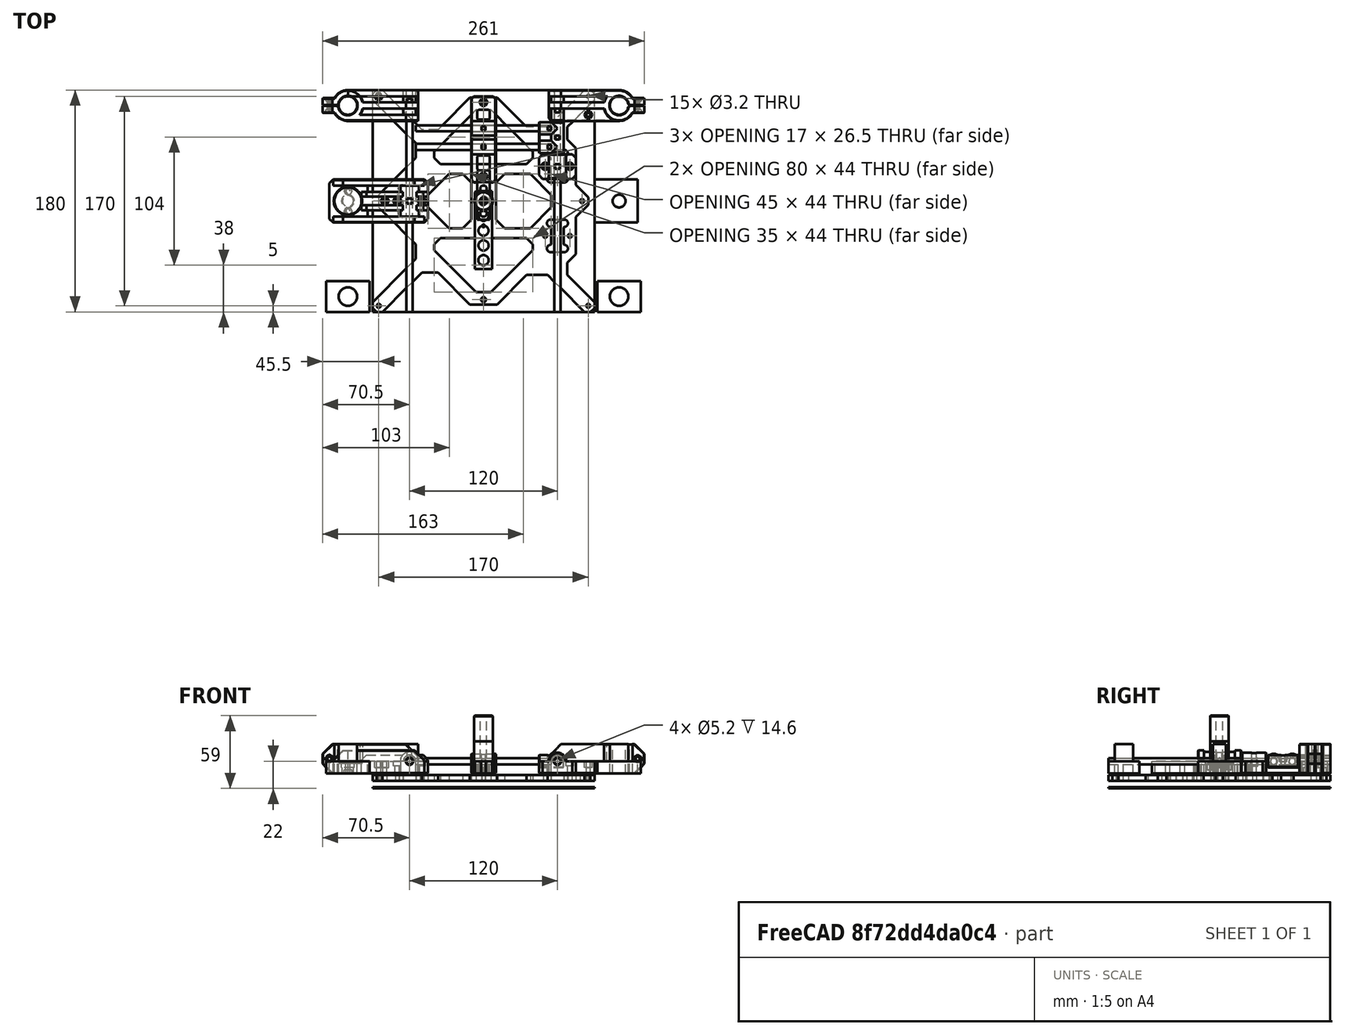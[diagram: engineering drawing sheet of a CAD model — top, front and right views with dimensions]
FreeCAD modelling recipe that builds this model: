
FCSTD DOCUMENT  (FreeCAD 0.18R16146 (Git))
Label: mini-bed
License: All rights reserved
LicenseURL: http://en.wikipedia.org/wiki/All_rights_reserved
objects: Part::Cylinder×73, Part::Chamfer×40, Part::Box×32, Part::Cut×28, Part::MultiFuse×22, Part::Feature×9
note: 204 computed .brp shape members not serialized (recipe doc carries the construction recipe); baked Part::Feature solids carry a one-line shape summary decoded from their .brp

FEATURE [Part::Feature] Part__Feature  label="carrier"
  Placement = pos=(0,0,-1) rot=(0,1,0;3.14159rad)
  shape: bbox 180 x 180 x 5 mm, 131 faces (baked)
FEATURE [Part::Cylinder] Cylinder
  Angle = 360
  AttacherType = Attacher::AttachEngine3D
  Height = 24
  Placement = pos=(-110,0,0) rot=(0,0,1;0rad)
  Radius = 4.5
FEATURE [Part::Cylinder] Cylinder001
  Angle = 360
  AttacherType = Attacher::AttachEngine3D
  Height = 24
  Placement = pos=(110,0,0) rot=(0,0,1;0rad)
  Radius = 5.2
FEATURE [Part::Cylinder] Cylinder002
  Angle = 360
  AttacherType = Attacher::AttachEngine3D
  Height = 24
  Placement = pos=(-110,77.5,0) rot=(0,0,1;0rad)
  Radius = 7.5
FEATURE [Part::Cylinder] Cylinder003
  Angle = 360
  AttacherType = Attacher::AttachEngine3D
  Height = 24
  Placement = pos=(-110,-77.5,0) rot=(0,0,1;0rad)
  Radius = 7.5
FEATURE [Part::Cylinder] Cylinder005
  Angle = 360
  AttacherType = Attacher::AttachEngine3D
  Height = 24
  Placement = pos=(110,-77.5,0) rot=(0,0,1;0rad)
  Radius = 7.5
FEATURE [Part::Cylinder] Cylinder007
  Angle = 360
  AttacherType = Attacher::AttachEngine3D
  Height = 30
  Placement = pos=(0,80,0) rot=(0,0,1;0rad)
  Radius = 1.65
FEATURE [Part::Cylinder] Cylinder008
  Angle = 360
  AttacherType = Attacher::AttachEngine3D
  Height = 10
  Placement = pos=(0,-80,0) rot=(0,0,1;0rad)
  Radius = 2
FEATURE [Part::Box] Box  label="bed"
  AttacherType = Attacher::AttachEngine3D
  Height = 1
  Length = 180
  Placement = pos=(-90,-90,-12) rot=(0,0,1;0rad)
  Width = 180
FEATURE [Part::Box] Box001  label="Cube"
  AttacherType = Attacher::AttachEngine3D
  Height = 10
  Length = 57
  Placement = pos=(-110,65,0) rot=(0,0,1;0rad)
  Width = 25
FEATURE [Part::Box] Box002  label="Cube001"
  AttacherType = Attacher::AttachEngine3D
  Height = 10
  Length = 35
  Placement = pos=(-127.5,-90,0) rot=(0,0,1;0rad)
  Width = 25
FEATURE [Part::Box] Box003  label="Cube002"
  AttacherType = Attacher::AttachEngine3D
  Height = 10
  Length = 35
  Placement = pos=(92.5,-90,0) rot=(0,0,1;0rad)
  Width = 25
FEATURE [Part::Box] Box005  label="Cube004"
  AttacherType = Attacher::AttachEngine3D
  Height = 10
  Length = 80
  Placement = pos=(-125,-17.5,0) rot=(0,0,1;0rad)
  Width = 35
FEATURE [Part::Box] Box006  label="Cube005"
  AttacherType = Attacher::AttachEngine3D
  Height = 10
  Length = 35
  Placement = pos=(90,-17.5,0) rot=(0,0,1;0rad)
  Width = 35
FEATURE [Part::Cylinder] Cylinder011
  Angle = 360
  AttacherType = Attacher::AttachEngine3D
  Height = 180
  Placement = pos=(-60,-90,10) rot=(-1,0,0;1.5708rad)
  Radius = 2.5
FEATURE [Part::Cylinder] Cylinder012
  Angle = 360
  AttacherType = Attacher::AttachEngine3D
  Height = 180
  Placement = pos=(60,-90,10) rot=(-1,0,0;1.5708rad)
  Radius = 2.5
FEATURE [Part::Cylinder] Cylinder013
  Angle = 360
  AttacherType = Attacher::AttachEngine3D
  Height = 24
  Placement = pos=(-110,77.5,0) rot=(0,0,1;0rad)
  Radius = 12.5
FEATURE [Part::Box] Box007  label="Cube006"
  AttacherType = Attacher::AttachEngine3D
  Height = 24
  Length = 57
  Placement = pos=(-110,65,0) rot=(0,0,1;0rad)
  Width = 5
FEATURE [Part::Box] Box008  label="Cube007"
  AttacherType = Attacher::AttachEngine3D
  Height = 24
  Length = 57
  Placement = pos=(-110,85,0) rot=(0,0,1;0rad)
  Width = 5
FEATURE [Part::Box] Box009  label="Cube008"
  AttacherType = Attacher::AttachEngine3D
  Height = 24
  Length = 49
  Placement = pos=(-102,75,0) rot=(0,0,1;0rad)
  Width = 5
FEATURE [Part::Cylinder] Cylinder014
  Angle = 360
  AttacherType = Attacher::AttachEngine3D
  Height = 25
  Placement = pos=(-60,65,10) rot=(-1,0,0;1.5708rad)
  Radius = 5
FEATURE [Part::Cylinder] Cylinder015
  Angle = 360
  AttacherType = Attacher::AttachEngine3D
  Height = 70
  Placement = pos=(-85,85,0) rot=(0,0,1;0rad)
  Radius = 1.65
FEATURE [Part::Box] Box010  label="Cube009"
  AttacherType = Attacher::AttachEngine3D
  Height = 24
  Length = 12
  Placement = pos=(-130.5,71.5,0) rot=(0,0,1;0rad)
  Width = 12
FEATURE [Part::Chamfer] Chamfer
  Base = -> Box007
  Edges = 1 edges r=10: [Edge6]
FEATURE [Part::Chamfer] Chamfer001
  Base = -> Box009
  Edges = 1 edges r=10: [Edge6]
FEATURE [Part::Chamfer] Chamfer002
  Base = -> Box010
  Edges = 2 edges r=8: [Edge2,Edge4]
FEATURE [Part::Chamfer] Chamfer003
  Base = -> Chamfer002
  Edges = 10 edges r=0.4: [Edge1,Edge4,Edge5,Edge6,Edge8,Edge9,Edge11,Edge13,Edge14,Edge16]
FEATURE [Part::Cylinder] Cylinder016
  Angle = 360
  AttacherType = Attacher::AttachEngine3D
  Height = 24
  Placement = pos=(-110,77.5,0) rot=(0,0,1;0rad)
  Radius = 7.5
FEATURE [Part::Feature] Body001  label="hex-nut"
  shape: bbox 5.543 x 6.4 x 5 mm, 8 faces (baked)
FEATURE [Part::Feature] Body002  label="hex-nut001"
  Placement = pos=(-85,85,5) rot=(0,0,-1;1.5708rad)
  shape: bbox 6.4 x 5.543 x 5 mm, 8 faces (baked)
FEATURE [Part::Feature] Body003  label="hex-nut002"
  Placement = pos=(-125,81,12) rot=(0,0.707107,0.707107;3.14159rad)
  shape: bbox 5.543 x 5 x 6.4 mm, 8 faces (baked)
FEATURE [Part::Cut] Cut
  Base = -> Chamfer003
  Tool = -> Body003
FEATURE [Part::Cut] Cut001
  Base = -> Box001
  Tool = -> Body002
FEATURE [Part::Cut] Cut002
  Base = -> Cut001
  Tool = -> Cylinder015
FEATURE [Part::Chamfer] Chamfer004
  Base = -> Cut002
  Edges = 1 edges r=2: [Edge17]
FEATURE [Part::Chamfer] Chamfer005
  Base = -> Cylinder013
  Edges = 2 edges r=0.4: [Edge1,Edge3]
FEATURE [Part::MultiFuse] Fusion001
  Shapes = -> [Chamfer004,Chamfer001,Chamfer]
FEATURE [Part::Chamfer] Chamfer006
  Base = -> Fusion001
  Edges = 11 edges r=0.4: [Edge16,Edge19,Edge31,Edge40,Edge59,Edge63,Edge64,Edge65,Edge67,Edge70,Edge76]
FEATURE [Part::Cylinder] Cylinder017
  Angle = 360
  AttacherType = Attacher::AttachEngine3D
  Height = 3
  Placement = pos=(-125,71,12) rot=(-1,0,0;1.5708rad)
  Radius = 3
FEATURE [Part::Cylinder] Cylinder018
  Angle = 360
  AttacherType = Attacher::AttachEngine3D
  Height = 21
  Placement = pos=(-125,68,12) rot=(-1,0,0;1.5708rad)
  Radius = 1.65
FEATURE [Part::Cylinder] Cylinder019
  Angle = 360
  AttacherType = Attacher::AttachEngine3D
  Height = 21
  Placement = pos=(-125,68,13.4) rot=(-1,0,0;1.5708rad)
  Radius = 0.5
FEATURE [Part::MultiFuse] Fusion002
  Shapes = -> [Cylinder019,Cylinder018]
FEATURE [Part::Cut] Cut003
  Base = -> Cut
  Tool = -> Fusion002
FEATURE [Part::Cylinder] Cylinder020
  Angle = 360
  AttacherType = Attacher::AttachEngine3D
  Height = 3
  Placement = pos=(-125,71,14.7) rot=(-1,0,0;1.5708rad)
  Radius = 0.5
FEATURE [Part::MultiFuse] Fusion003
  Shapes = -> [Cylinder020,Cylinder017]
FEATURE [Part::Cut] Cut004
  Base = -> Cut003
  Tool = -> Fusion003
FEATURE [Part::Box] Box012  label="Cube011"
  AttacherType = Attacher::AttachEngine3D
  Height = 36
  Length = 22
  Placement = pos=(-135,77.25,0) rot=(0,0,1;0rad)
  Width = 0.5
FEATURE [Part::Cylinder] Cylinder021  label="rod-slot-1"
  Angle = 360
  AttacherType = Attacher::AttachEngine3D
  Height = 25
  Placement = pos=(-60,65,10) rot=(-1,0,0;1.5708rad)
  Radius = 2.6
FEATURE [Part::Cylinder] Cylinder022
  Angle = 360
  AttacherType = Attacher::AttachEngine3D
  Height = 3
  Placement = pos=(-60,80,10) rot=(-1,0,0;1.5708rad)
  Radius = 3
FEATURE [Part::Box] Box013  label="Cube012"
  AttacherType = Attacher::AttachEngine3D
  Height = 10
  Length = 4
  Placement = pos=(-62,80,9) rot=(0,0,1;0rad)
  Width = 3
FEATURE [Part::Cylinder] Cylinder023
  Angle = 360
  AttacherType = Attacher::AttachEngine3D
  Height = 27
  Placement = pos=(-80,0,0) rot=(0,0,1;0rad)
  Radius = 1.65
FEATURE [Part::Cylinder] Cylinder024
  Angle = 360
  AttacherType = Attacher::AttachEngine3D
  Height = 27
  Placement = pos=(-70,0,0) rot=(0,0,1;0rad)
  Radius = 1.65
FEATURE [Part::Cylinder] Cylinder025
  Angle = 360
  AttacherType = Attacher::AttachEngine3D
  Height = 27
  Placement = pos=(-50,0,0) rot=(0,0,1;0rad)
  Radius = 1.65
FEATURE [Part::Cylinder] Cylinder026
  Angle = 360
  AttacherType = Attacher::AttachEngine3D
  Height = 2
  Placement = pos=(-110,0,8) rot=(0,0,1;0rad)
  Radius = 11.5
FEATURE [Part::Cylinder] Cylinder027
  Angle = 360
  AttacherType = Attacher::AttachEngine3D
  Height = 10
  Placement = pos=(-110,8,0) rot=(0,0,1;0rad)
  Radius = 1.65
FEATURE [Part::Cylinder] Cylinder028
  Angle = 360
  AttacherType = Attacher::AttachEngine3D
  Height = 10
  Placement = pos=(-110,-8,0) rot=(0,0,1;0rad)
  Radius = 1.65
FEATURE [Part::Feature] Body004  label="hex-nut003"
  Placement = pos=(-110,8,-2) rot=(0,0,-1;4.71239rad)
  shape: bbox 6.4 x 5.543 x 5 mm, 8 faces (baked)
FEATURE [Part::Feature] Body005  label="hex-nut004"
  Placement = pos=(-110,-8,-2) rot=(0,0,1;1.5708rad)
  shape: bbox 6.4 x 5.543 x 5 mm, 8 faces (baked)
FEATURE [Part::Cylinder] Cylinder029
  Angle = 360
  AttacherType = Attacher::AttachEngine3D
  Height = 24
  Placement = pos=(-110,0,5) rot=(0,0,1;0rad)
  Radius = 5.2
FEATURE [Part::Cut] Cut009
  Base = -> Box005
  Tool = -> Cylinder029
FEATURE [Part::Cylinder] Cylinder030
  Angle = 360
  AttacherType = Attacher::AttachEngine3D
  Height = 35
  Placement = pos=(-60,-17.5,10) rot=(-1,0,0;1.5708rad)
  Radius = 7.5
FEATURE [Part::Cylinder] Cylinder031  label="rod-slot-2"
  Angle = 360
  AttacherType = Attacher::AttachEngine3D
  Height = 35
  Placement = pos=(-60,-17.5,10) rot=(-1,0,0;1.5708rad)
  Radius = 2.6
FEATURE [Part::Box] Box014  label="Cube013"
  AttacherType = Attacher::AttachEngine3D
  Height = 5
  Length = 54
  Placement = pos=(-99,-7.5,10) rot=(0,0,1;0rad)
  Width = 4
FEATURE [Part::Box] Box015  label="Cube014"
  AttacherType = Attacher::AttachEngine3D
  Height = 9
  Length = 74
  Placement = pos=(-122,12.5,10) rot=(0,0,1;0rad)
  Width = 5
FEATURE [Part::Feature] Body006  label="hex-nut005"
  Placement = pos=(-80,0,5) rot=(0,0,-1;1.5708rad)
  shape: bbox 6.4 x 5.543 x 5 mm, 8 faces (baked)
FEATURE [Part::Box] Box016  label="Cube015"
  AttacherType = Attacher::AttachEngine3D
  Height = 9
  Length = 74
  Placement = pos=(-122,-17.5,10) rot=(0,0,1;0rad)
  Width = 5
FEATURE [Part::Box] Box017  label="Cube016"
  AttacherType = Attacher::AttachEngine3D
  Height = 5
  Length = 54
  Placement = pos=(-99,3.5,10) rot=(0,0,1;0rad)
  Width = 4
FEATURE [Part::Chamfer] Chamfer012
  Base = -> Box015
  Edges = 2 edges r=8: [Edge2,Edge6]
FEATURE [Part::Chamfer] Chamfer013
  Base = -> Box016
  Edges = 2 edges r=8: [Edge2,Edge6]
FEATURE [Part::Chamfer] Chamfer014
  Base = -> Box017
  Edges = 2 edges r=4: [Edge2,Edge6]
FEATURE [Part::Chamfer] Chamfer015
  Base = -> Box014
  Edges = 2 edges r=4: [Edge2,Edge6]
FEATURE [Part::Chamfer] Chamfer016
  Base = -> Chamfer013
  Edges = 5 edges r=0.4: [Edge1,Edge5,Edge6,Edge8,Edge9]
FEATURE [Part::Chamfer] Chamfer017
  Base = -> Chamfer012
  Edges = 5 edges r=0.4: [Edge4,Edge11,Edge14,Edge15,Edge16]
FEATURE [Part::Cylinder] Cylinder032
  Angle = 360
  AttacherType = Attacher::AttachEngine3D
  Height = 12
  Placement = pos=(-70,0,6) rot=(0,0,1;0rad)
  Radius = 3
FEATURE [Part::Cylinder] Cylinder033
  Angle = 360
  AttacherType = Attacher::AttachEngine3D
  Height = 12
  Placement = pos=(-50,0,6) rot=(0,0,1;0rad)
  Radius = 3
FEATURE [Part::Cylinder] Cylinder034
  Angle = 360
  AttacherType = Attacher::AttachEngine3D
  Height = 5
  Placement = pos=(-60,-2.5,10) rot=(-1,0,0;1.5708rad)
  Radius = 3
FEATURE [Part::MultiFuse] Fusion009
  Shapes = -> [Box013,Cylinder022]
FEATURE [Part::Box] Box018  label="Cube017"
  AttacherType = Attacher::AttachEngine3D
  Height = 10
  Length = 4
  Placement = pos=(-62,-2,11) rot=(0,0,1;0rad)
  Width = 4
FEATURE [Part::Cylinder] Cylinder035
  Angle = 360
  AttacherType = Attacher::AttachEngine3D
  Height = 4
  Placement = pos=(50,28.25,0) rot=(0,0,1;0rad)
  Radius = 3
FEATURE [Part::Cylinder] Cylinder036
  Angle = 360
  AttacherType = Attacher::AttachEngine3D
  Height = 4
  Placement = pos=(70,28.25,0) rot=(0,0,1;0rad)
  Radius = 3
FEATURE [Part::Box] Box019  label="Cube018"
  AttacherType = Attacher::AttachEngine3D
  Height = 10
  Length = 30
  Placement = pos=(45,18,0) rot=(0,0,1;0rad)
  Width = 20
FEATURE [Part::Cylinder] Cylinder037
  Angle = 360
  AttacherType = Attacher::AttachEngine3D
  Height = 20
  Placement = pos=(60,18,10) rot=(-1,0,0;1.5708rad)
  Radius = 7
FEATURE [Part::Cylinder] Cylinder038  label="rod-slot-3"
  Angle = 360
  AttacherType = Attacher::AttachEngine3D
  Height = 20
  Placement = pos=(60,18,10) rot=(-1,0,0;1.5708rad)
  Radius = 2.6
FEATURE [Part::Chamfer] Chamfer019
  Base = -> Box019
  Edges = 4 edges r=3: [Edge1,Edge3,Edge5,Edge7]
FEATURE [Part::Cylinder] Cylinder039
  Angle = 360
  AttacherType = Attacher::AttachEngine3D
  Height = 33
  Placement = pos=(50,28.25,0) rot=(0,0,1;0rad)
  Radius = 1.65
FEATURE [Part::Cylinder] Cylinder040
  Angle = 360
  AttacherType = Attacher::AttachEngine3D
  Height = 33
  Placement = pos=(70,28.25,0) rot=(0,0,1;0rad)
  Radius = 1.65
FEATURE [Part::MultiFuse] Fusion010
  Shapes = -> [Cylinder040,Cylinder039]
FEATURE [Part::Cut] Cut024
  Base = -> Chamfer019
  Tool = -> Fusion010
FEATURE [Part::MultiFuse] Fusion011
  Placement = pos=(0,0,6) rot=(0,0,1;0rad)
  Shapes = -> [Cylinder035,Cylinder036]
FEATURE [Part::Chamfer] Chamfer020
  Base = -> Cylinder037
  Edges = 2 edges r=0.4: [Edge1,Edge3]
FEATURE [Part::Chamfer] Chamfer021
  Base = -> Cut024
  Edges = 10 edges r=0.4: [Edge4,Edge14,Edge16,Edge18,Edge19,Edge20,Edge21,Edge22,Edge23,Edge24]
FEATURE [Part::Cut] Cut025
  Base = -> Chamfer021
  Tool = -> Fusion011
FEATURE [Part::MultiFuse] Fusion012
  Shapes = -> [Cut025,Chamfer020]
FEATURE [Part::Cylinder] Cylinder041  label="cut"
  Angle = 360
  AttacherType = Attacher::AttachEngine3D
  Height = 4
  Placement = pos=(60,26.25,10) rot=(-1,0,0;1.5708rad)
  Radius = 3
FEATURE [Part::Box] Box020  label="Cube019"
  AttacherType = Attacher::AttachEngine3D
  Height = 10
  Length = 4
  Placement = pos=(58,26,10) rot=(0,0,1;0rad)
  Width = 4
FEATURE [Part::Cut] Cut026
  Base = -> Fusion012
  Tool = -> Cylinder041
FEATURE [Part::Cut] Cut027
  Base = -> Cut026
  Tool = -> Box020
FEATURE [Part::Chamfer] Chamfer007
  Base = -> Cylinder014
  Edges = 1 edges r=0.4: [Edge1]
FEATURE [Part::MultiFuse] Fusion006
  Shapes = -> [Chamfer005,Chamfer006,Chamfer007,Cut004]
FEATURE [Part::Cut] Cut005
  Base = -> Fusion006
  Tool = -> Cylinder016
FEATURE [Part::Cut] Cut006
  Base = -> Cut005
  Tool = -> Box012
FEATURE [Part::Chamfer] Chamfer008
  Base = -> Cut006
  Edges = 2 edges r=1: [Edge33,Edge49]
FEATURE [Part::Chamfer] Chamfer009
  Base = -> Chamfer008
  Edges = 11 edges r=0.4: [Edge2,Edge4,Edge21,Edge23,Edge24,Edge26,Edge55,Edge59,Edge61,Edge62,Edge102]
FEATURE [Part::Cut] Cut021
  Base = -> Chamfer009
  Tool = -> Fusion009
FEATURE [Part::Cylinder] Cylinder042  label="Cylinder041"
  Angle = 360
  AttacherType = Attacher::AttachEngine3D
  Height = 26.5
  Radius = 7.5
FEATURE [Part::Cylinder] Cylinder043  label="Cylinder042"
  Angle = 360
  AttacherType = Attacher::AttachEngine3D
  Height = 26.5
  Radius = 2.65
FEATURE [Part::Cylinder] Cylinder044  label="Cylinder045"
  Angle = 360
  AttacherType = Attacher::AttachEngine3D
  Height = 47
  Radius = 2.65
FEATURE [Part::Cylinder] Cylinder045  label="Cylinder046"
  Angle = 360
  AttacherType = Attacher::AttachEngine3D
  Height = 47
  Radius = 7.5
FEATURE [Part::Cut] Cut031
  Base = -> Cylinder045
  Tool = -> Cylinder044
FEATURE [Part::Chamfer] Chamfer025  label="long-rod"
  Base = -> Cut031
  Edges = 4 edges r=0.4: [Edge1,Edge3,Edge4,Edge5]
FEATURE [Part::Cut] Cut032
  Base = -> Cylinder042
  Tool = -> Cylinder043
FEATURE [Part::Chamfer] Chamfer026  label="short-rod"
  Base = -> Cut032
  Edges = 4 edges r=0.4: [Edge1,Edge3,Edge4,Edge5]
FEATURE [Part::MultiFuse] Fusion013
  Shapes = -> [Cylinder034,Box018]
FEATURE [Part::MultiFuse] Fusion014
  Shapes = -> [Body004,Cylinder027,Cylinder,Body005,Cylinder028,Cylinder026]
FEATURE [Part::Chamfer] Chamfer027
  Base = -> Cut009
  Edges = 4 edges r=3: [Edge1,Edge3,Edge6,Edge12]
FEATURE [Part::Chamfer] Chamfer028
  Base = -> Chamfer027
  Edges = 8 edges r=0.4: [Edge4,Edge13,Edge15,Edge17,Edge18,Edge19,Edge20,Edge21]
FEATURE [Part::MultiFuse] Fusion016
  Shapes = -> [Chamfer028,Chamfer017,Chamfer014,Cylinder030,Chamfer015,Chamfer016]
FEATURE [Part::Cut] Cut033
  Base = -> Fusion016
  Tool = -> Fusion014
FEATURE [Part::Box] Box021  label="Cube020"
  AttacherType = Attacher::AttachEngine3D
  Height = 10
  Length = 27
  Placement = pos=(-94,7.5,0) rot=(0,0,1;0rad)
  Width = 5
FEATURE [Part::Box] Box022  label="Cube021"
  AttacherType = Attacher::AttachEngine3D
  Height = 10
  Length = 27
  Placement = pos=(-94,-12.5,0) rot=(0,0,1;0rad)
  Width = 5
FEATURE [Part::MultiFuse] Fusion017
  Shapes = -> [Box022,Box021]
FEATURE [Part::Cylinder] Cylinder047
  Angle = 360
  AttacherType = Attacher::AttachEngine3D
  Height = 10
  Placement = pos=(0,10,0) rot=(0,0,1;0rad)
  Radius = 2.6
FEATURE [Part::Cylinder] Cylinder048
  Angle = 360
  AttacherType = Attacher::AttachEngine3D
  Height = 10
  Radius = 2.65
FEATURE [Part::Cylinder] Cylinder049
  Angle = 360
  AttacherType = Attacher::AttachEngine3D
  Height = 10
  Placement = pos=(0,-10,0) rot=(0,0,1;0rad)
  Radius = 2.7
FEATURE [Part::Cylinder] Cylinder050
  Angle = 360
  AttacherType = Attacher::AttachEngine3D
  Height = 10
  Placement = pos=(0,20,0) rot=(0,0,1;0rad)
  Radius = 2.55
FEATURE [Part::Box] Box023  label="Cube022"
  AttacherType = Attacher::AttachEngine3D
  Height = 10
  Length = 10
  Placement = pos=(-5,-15,0) rot=(0,0,1;0rad)
  Width = 40
FEATURE [Part::MultiFuse] Fusion020
  Shapes = -> [Cylinder050,Cylinder047,Cylinder049,Cylinder048]
FEATURE [Part::Chamfer] Chamfer029
  Base = -> Box023
  Edges = 1 edges r=1: [Edge3]
FEATURE [Part::Cut] Cut038  label="cf-rod-size-test-255-270"
  Base = -> Chamfer029
  Tool = -> Fusion020
FEATURE [Part::Cylinder] Cylinder051
  Angle = 360
  AttacherType = Attacher::AttachEngine3D
  Height = 10
  Radius = 4
FEATURE [Part::Cylinder] Cylinder052
  Angle = 360
  AttacherType = Attacher::AttachEngine3D
  Height = 10
  Placement = pos=(0,-12,0) rot=(0,0,1;0rad)
  Radius = 4.05
FEATURE [Part::Cylinder] Cylinder053
  Angle = 360
  AttacherType = Attacher::AttachEngine3D
  Height = 10
  Placement = pos=(0,-24,0) rot=(0,0,1;0rad)
  Radius = 4.1
FEATURE [Part::Cylinder] Cylinder054
  Angle = 360
  AttacherType = Attacher::AttachEngine3D
  Height = 10
  Placement = pos=(0,-36,0) rot=(0,0,1;0rad)
  Radius = 4.15
FEATURE [Part::Cylinder] Cylinder055
  Angle = 360
  AttacherType = Attacher::AttachEngine3D
  Height = 10
  Placement = pos=(0,-48,0) rot=(0,0,1;0rad)
  Radius = 4.2
FEATURE [Part::Box] Box024  label="Cube023"
  AttacherType = Attacher::AttachEngine3D
  Height = 10
  Length = 14
  Placement = pos=(-7,-55,0) rot=(0,0,1;0rad)
  Width = 63
FEATURE [Part::Chamfer] Chamfer030
  Base = -> Box024
  Edges = 1 edges r=1: [Edge3]
FEATURE [Part::MultiFuse] Fusion021
  Shapes = -> [Cylinder055,Cylinder051,Cylinder054,Cylinder052,Cylinder053]
FEATURE [Part::Cut] Cut039  label="shaft-rod-size-test-400-420"
  Base = -> Chamfer030
  Tool = -> Fusion021
FEATURE [Part::Cut] Cut041
  Base = -> Cut021
  Tool = -> Cylinder021
FEATURE [Part::Chamfer] Chamfer032  label="corner-r1"
  Base = -> Cut041
  Edges = 4 edges r=0.4: [Edge167,Edge172,Edge313,Edge358]
FEATURE [Part::Cut] Cut043
  Base = -> Cut027
  Tool = -> Cylinder038
FEATURE [Part::Chamfer] Chamfer034  label="node-r1"
  Base = -> Cut043
  Edges = 4 edges r=0.4: [Edge63,Edge76,Edge78,Edge91]
FEATURE [Part::Cylinder] Cylinder056
  Angle = 360
  AttacherType = Attacher::AttachEngine3D
  Height = 10
  Radius = 1
FEATURE [Part::Cylinder] Cylinder057
  Angle = 360
  AttacherType = Attacher::AttachEngine3D
  Height = 30
  Placement = pos=(0,20,0) rot=(0,0,1;0rad)
  Radius = 1.65
FEATURE [Part::Cylinder] Cylinder058
  Angle = 360
  AttacherType = Attacher::AttachEngine3D
  Height = 10
  Placement = pos=(0,-20,0) rot=(0,0,1;0rad)
  Radius = 1
FEATURE [Part::Box] Box025  label="Cube024"
  AttacherType = Attacher::AttachEngine3D
  Height = 10
  Length = 20
  Placement = pos=(-10,15,0) rot=(0,0,1;0rad)
  Width = 70
FEATURE [Part::Cylinder] Cylinder059
  Angle = 360
  AttacherType = Attacher::AttachEngine3D
  Height = 20
  Placement = pos=(-10,59,10) rot=(0,1,0;1.5708rad)
  Radius = 2.6
FEATURE [Part::Cylinder] Cylinder060
  Angle = 360
  AttacherType = Attacher::AttachEngine3D
  Height = 20
  Placement = pos=(-10,44,10) rot=(0,1,0;1.5708rad)
  Radius = 6
FEATURE [Part::Cylinder] Cylinder061
  Angle = 360
  AttacherType = Attacher::AttachEngine3D
  Height = 20
  Placement = pos=(-10,59,10) rot=(0,1,0;1.5708rad)
  Radius = 6
FEATURE [Part::Feature] Body007  label="hex-nut006"
  Placement = pos=(0,80,5) rot=(0,0,1;0.523599rad)
  shape: bbox 6.4 x 5.543 x 5 mm, 8 faces (baked)
FEATURE [Part::MultiFuse] Fusion022
  Shapes = -> [Body006,Cylinder023,Cylinder032,Cylinder024,Cylinder033,Cylinder025]
FEATURE [Part::Cut] Cut044
  Base = -> Cut033
  Tool = -> Fusion017
FEATURE [Part::Cut] Cut045
  Base = -> Cut044
  Tool = -> Fusion013
FEATURE [Part::Cut] Cut046
  Base = -> Cut045
  Tool = -> Fusion022
FEATURE [Part::Cut] Cut047
  Base = -> Cut046
  Tool = -> Cylinder031
FEATURE [Part::Chamfer] Chamfer035  label="middle-r1"
  Base = -> Cut047
  Edges = 4 edges r=0.4: [Edge2,Edge5,Edge305,Edge311]
FEATURE [Part::Cylinder] Cylinder062
  Angle = 360
  AttacherType = Attacher::AttachEngine3D
  Height = 20
  Placement = pos=(-10,44,10) rot=(0,1,0;1.5708rad)
  Radius = 2.6
FEATURE [Part::Cylinder] Cylinder063
  Angle = 360
  AttacherType = Attacher::AttachEngine3D
  Height = 5
  Placement = pos=(0,20,7) rot=(0,0,1;0rad)
  Radius = 3
FEATURE [Part::Chamfer] Chamfer036
  Base = -> Box025
  Edges = 4 edges r=2: [Edge1,Edge3,Edge5,Edge7]
FEATURE [Part::Chamfer] Chamfer037
  Base = -> Cylinder061
  Edges = 2 edges r=0.4: [Edge1,Edge3]
FEATURE [Part::Chamfer] Chamfer038
  Base = -> Cylinder060
  Edges = 2 edges r=0.4: [Edge1,Edge3]
FEATURE [Part::Chamfer] Chamfer039
  Base = -> Chamfer036
  Edges = 16 edges r=0.4: [Edge1,Edge4,Edge5,Edge6,Edge7,Edge8,Edge9,Edge10,Edge11,Edge12,Edge14,Edge16,Edge17,Edge18,Edge19,Edge20]
FEATURE [Part::MultiFuse] Fusion023
  Shapes = -> [Cylinder063,Cylinder057,Cylinder007,Body007]
FEATURE [Part::Cut] Cut048
  Base = -> Chamfer039
  Tool = -> Fusion023
FEATURE [Part::MultiFuse] Fusion024
  Shapes = -> [Cut048,Chamfer037,Chamfer038]
FEATURE [Part::Feature] Chamfer032001  label="corner-r002"
  Placement = pos=(1.9e-14,155,0) rot=(0,0,1;3.14159rad)
  shape: bbox 77.5 x 25 x 24 mm, 155 faces (baked)
FEATURE [Part::Box] Box026  label="Cube025"
  AttacherType = Attacher::AttachEngine3D
  Height = 5
  Length = 20
  Placement = pos=(45,39,5) rot=(0,0,1;0rad)
  Width = 25
FEATURE [Part::Cylinder] Cylinder064
  Angle = 360
  AttacherType = Attacher::AttachEngine3D
  Height = 10
  Placement = pos=(45,44,10) rot=(0,1,0;1.5708rad)
  Radius = 2.6
FEATURE [Part::Cylinder] Cylinder065
  Angle = 360
  AttacherType = Attacher::AttachEngine3D
  Height = 10
  Placement = pos=(45,59,10) rot=(0,1,0;1.5708rad)
  Radius = 2.6
FEATURE [Part::Cylinder] Cylinder066  label="rod-slot-004"
  Angle = 360
  AttacherType = Attacher::AttachEngine3D
  Height = 25
  Placement = pos=(60,39,10) rot=(-1,0,0;1.5708rad)
  Radius = 2.6
FEATURE [Part::Cylinder] Cylinder067
  Angle = 360
  AttacherType = Attacher::AttachEngine3D
  Height = 15
  Placement = pos=(45,59,10) rot=(0,1,0;1.5708rad)
  Radius = 5
FEATURE [Part::Cylinder] Cylinder068
  Angle = 360
  AttacherType = Attacher::AttachEngine3D
  Height = 15
  Placement = pos=(45,44,10) rot=(0,1,0;1.5708rad)
  Radius = 5
FEATURE [Part::Cylinder] Cylinder069  label="rod-slot-005"
  Angle = 360
  AttacherType = Attacher::AttachEngine3D
  Height = 25
  Placement = pos=(60,39,10) rot=(-1,0,0;1.5708rad)
  Radius = 5
FEATURE [Part::Chamfer] Chamfer032003
  Base = -> Cylinder069
  Edges = 2 edges r=0.4: [Edge1,Edge3]
FEATURE [Part::Chamfer] Chamfer032005
  Base = -> Cylinder068
  Edges = 1 edges r=0.4: [Edge3]
FEATURE [Part::Chamfer] Chamfer032004
  Base = -> Cylinder067
  Edges = 1 edges r=0.4: [Edge3]
FEATURE [Part::Box] Box027  label="Cube026"
  AttacherType = Attacher::AttachEngine3D
  Height = 10
  Length = 10
  Placement = pos=(-5,25,0) rot=(0,0,1;0rad)
  Width = 12
FEATURE [Part::Box] Box028  label="Cube027"
  AttacherType = Attacher::AttachEngine3D
  Height = 10
  Length = 10
  Placement = pos=(-5,66,0) rot=(0,0,1;0rad)
  Width = 8
FEATURE [Part::Chamfer] Chamfer032010
  Base = -> Box026
  Edges = 9 edges r=0.4: [Edge1,Edge2,Edge3,Edge4,Edge5,Edge7,Edge8,Edge9,Edge11]
FEATURE [Part::MultiFuse] Fusion030
  Shapes = -> [Chamfer032010,Chamfer032005,Chamfer032003,Chamfer032004]
FEATURE [Part::Cylinder] Cylinder070
  Angle = 360
  AttacherType = Attacher::AttachEngine3D
  Height = 3
  Placement = pos=(52,44,10) rot=(0,1,0;1.5708rad)
  Radius = 2.7
FEATURE [Part::Cylinder] Cylinder071
  Angle = 360
  AttacherType = Attacher::AttachEngine3D
  Height = 3
  Placement = pos=(52,59,10) rot=(0,1,0;1.5708rad)
  Radius = 2.7
FEATURE [Part::Cylinder] Cylinder072  label="rod-slot-006"
  Angle = 360
  AttacherType = Attacher::AttachEngine3D
  Height = 3
  Placement = pos=(60,50,10) rot=(-1,0,0;1.5708rad)
  Radius = 2.7
FEATURE [Part::Box] Box029  label="Cube028"
  AttacherType = Attacher::AttachEngine3D
  Height = 10
  Length = 3
  Placement = pos=(52,57.5,10) rot=(0,0,1;0rad)
  Width = 3
FEATURE [Part::Box] Box030  label="Cube029"
  AttacherType = Attacher::AttachEngine3D
  Height = 10
  Length = 3
  Placement = pos=(52,42.5,10) rot=(0,0,1;0rad)
  Width = 3
FEATURE [Part::Box] Box031  label="Cube030"
  AttacherType = Attacher::AttachEngine3D
  Height = 10
  Length = 3
  Placement = pos=(58.5,50,10) rot=(0,0,1;0rad)
  Width = 3
FEATURE [Part::MultiFuse] Fusion031
  Shapes = -> [Cylinder066,Cylinder065,Cylinder064,Cylinder070,Cylinder071,Cylinder072,Box029,Box030,Box031]
FEATURE [Part::Cut] Cut052
  Base = -> Fusion030
  Tool = -> Fusion031
FEATURE [Part::Chamfer] Chamfer032011  label="rf-r1"
  Base = -> Cut052
  Edges = 10 edges r=0.4: [Edge10,Edge11,Edge24,Edge40,Edge58,Edge59,Edge74,Edge105,Edge172,Edge183]
FEATURE [Part::Cylinder] Cylinder073
  Angle = 360
  AttacherType = Attacher::AttachEngine3D
  Height = 3
  Placement = pos=(-10,59,10) rot=(0,1,0;1.5708rad)
  Radius = 2.7
FEATURE [Part::Cylinder] Cylinder074
  Angle = 360
  AttacherType = Attacher::AttachEngine3D
  Height = 3
  Placement = pos=(-10,44,10) rot=(0,1,0;1.5708rad)
  Radius = 2.7
FEATURE [Part::MultiFuse] Fusion032
  Placement = pos=(8.5,0,0) rot=(0,0,1;0rad)
  Shapes = -> [Cylinder074,Cylinder073]
FEATURE [Part::Box] Box032  label="Cube031"
  AttacherType = Attacher::AttachEngine3D
  Height = 10
  Length = 3
  Placement = pos=(-1.5,42.5,10) rot=(0,0,1;0rad)
  Width = 3
FEATURE [Part::Box] Box033  label="Cube032"
  AttacherType = Attacher::AttachEngine3D
  Height = 10
  Length = 3
  Placement = pos=(-1.5,57.5,10) rot=(0,0,1;0rad)
  Width = 3
FEATURE [Part::MultiFuse] Fusion033
  Shapes = -> [Box033,Box032,Fusion032,Cylinder062,Cylinder059]
FEATURE [Part::Cut] Cut053
  Base = -> Fusion024
  Tool = -> Fusion033
FEATURE [Part::Chamfer] Chamfer032012
  Base = -> Box027
  Edges = 4 edges r=1: [Edge1,Edge3,Edge5,Edge7]
FEATURE [Part::Chamfer] Chamfer032013
  Base = -> Box028
  Edges = 4 edges r=1: [Edge1,Edge3,Edge5,Edge7]
FEATURE [Part::MultiFuse] Fusion034
  Shapes = -> [Chamfer032013,Chamfer032012]
FEATURE [Part::Cut] Cut054
  Base = -> Cut053
  Tool = -> Fusion034
FEATURE [Part::Chamfer] Chamfer032014  label="head-tail-r1"
  Base = -> Cut054
  Edges = 28 edges r=0.4: [Edge18,Edge19,Edge25,Edge26,Edge59,Edge69,Edge105,Edge106,Edge107,Edge108,Edge109,Edge110,Edge111,Edge112,Edge113,Edge114,Edge115,Edge116,Edge117,Edge118,Edge119,Edge120,Edge225,Edge226,Edge229,Edge230,Edge232,Edge238]
FEATURE [Part::Cylinder] Cylinder075
  Angle = 360
  AttacherType = Attacher::AttachEngine3D
  Height = 110
  Placement = pos=(-55,59,10) rot=(0,1,0;1.5708rad)
  Radius = 2.5
FEATURE [Part::Cylinder] Cylinder076
  Angle = 360
  AttacherType = Attacher::AttachEngine3D
  Height = 110
  Placement = pos=(-55,44,10) rot=(0,1,0;1.5708rad)
  Radius = 2.5
FEATURE [Part::Cylinder] Cylinder077
  Angle = 360
  AttacherType = Attacher::AttachEngine3D
  Height = 10
  Placement = pos=(-110,0,0) rot=(0,0,1;0rad)
  Radius = 11
